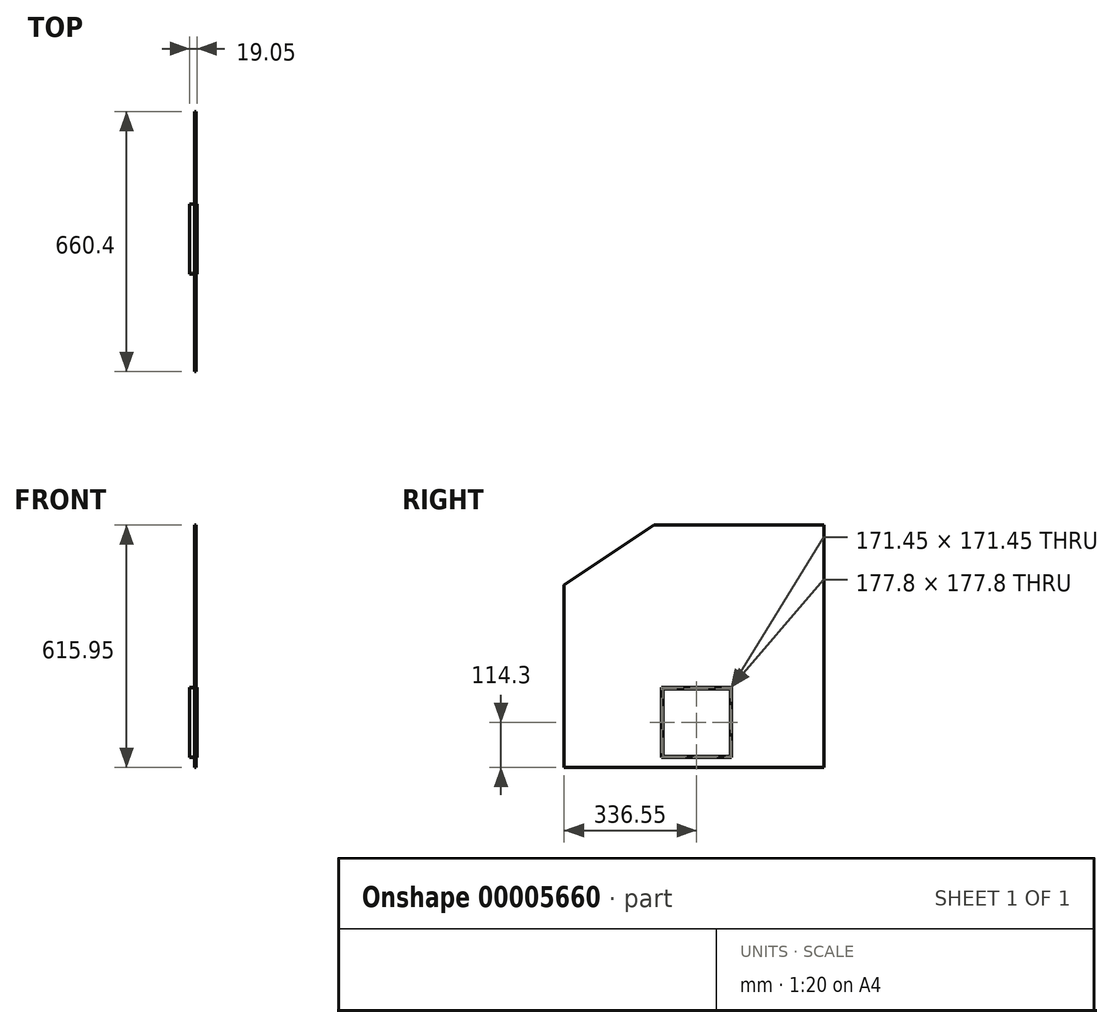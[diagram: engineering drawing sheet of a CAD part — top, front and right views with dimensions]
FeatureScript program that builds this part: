
annotation { "Feature Type Name" : "Feature", "Feature Type Description" : "" }
export const myFeature = defineFeature(function(context is Context, id is Id, definition is map)
    precondition{}
    {
        {
            var Q0;
            Q0=qCreatedBy(makeId("Right.planeOp"),FACE);
            var sketch = newSketch(context, id + "F0", { "sketchPlane" : qUnion([Q0])});
            skLineSegment(sketch, "E0.bottom", {"start": v(0, 0) * mm, "end": v(-431.8, 0) * mm});
            skLineSegment(sketch, "E0.top", {"start": v(0, 615.95) * mm, "end": v(-431.8, 615.95) * mm});
            skLineSegment(sketch, "E0.left", {"start": v(0, 0) * mm, "end": v(0, 615.95) * mm});
            skLineSegment(sketch, "E0.right", {"start": v(-431.8, 0) * mm, "end": v(-431.8, 615.95) * mm, "construction": true});
            skLineSegment(sketch, "E1", {"start": v(-431.8, 615.95) * mm, "end": v(-660.4, 463.55) * mm});
            skLineSegment(sketch, "E2", {"start": v(-660.4, 463.55) * mm, "end": v(-431.8, 463.55) * mm, "construction": true});
            skLineSegment(sketch, "E3", {"start": v(-660.4, 463.55) * mm, "end": v(-660.4, 0) * mm});
            skLineSegment(sketch, "E4", {"start": v(-431.8, 0) * mm, "end": v(-660.4, 0) * mm});
            skLineSegment(sketch, "E5.bottom", {"start": v(-234.95, 25.4) * mm, "end": v(-412.75, 25.4) * mm});
            skLineSegment(sketch, "E5.top", {"start": v(-234.95, 203.2) * mm, "end": v(-412.75, 203.2) * mm});
            skLineSegment(sketch, "E5.left", {"start": v(-234.95, 25.4) * mm, "end": v(-234.95, 203.2) * mm});
            skLineSegment(sketch, "E5.right", {"start": v(-412.75, 25.4) * mm, "end": v(-412.75, 203.2) * mm});
            skLineSegment(sketch, "E6.bottom", {"start": v(-238.12, 200.02) * mm, "end": v(-409.58, 200.02) * mm});
            skLineSegment(sketch, "E6.top", {"start": v(-238.12, 28.57) * mm, "end": v(-409.57, 28.57) * mm});
            skLineSegment(sketch, "E6.left", {"start": v(-238.12, 200.03) * mm, "end": v(-238.12, 28.57) * mm});
            skLineSegment(sketch, "E6.right", {"start": v(-409.57, 200.02) * mm, "end": v(-409.57, 28.57) * mm});
            skSolve(sketch);
        }
        {
            var Q0;
            Q0=qSketchRegion(id+"F0",true);
            extrude(context, id + "F1", {"entities" : qUnion([Q0]), "depth" : 3.17 * mm});
        }
        {
            var Q0;
            Q0=makeQuery(id+"F0.imprint","IMPRINT",FACE,{"disambiguationData":[TD([[makeQuery(id+"F0.imprint","IMPRINT",EDGE,{"derivedFrom":sQuery(id+"F0.wireOp",EDGE,"E6.bottom")}),1.0]])]});
            extrude(context, id + "F2", {"entities" : qUnion([Q0]), "operationType" : NewBodyOperationType.REMOVE, "oppositeDirection" : true, "depth" : 25.4 * mm});
        }
        {
            var Q0;
            Q0=makeQuery(id+"F0.imprint","IMPRINT",FACE,{"disambiguationData":[TD([[makeQuery(id+"F0.imprint","IMPRINT",EDGE,{"derivedFrom":sQuery(id+"F0.wireOp",EDGE,"E5.bottom")}),-1.0]])]});
            extrude(context, id + "F3", {"entities" : qUnion([Q0]), "endBound" : BoundingType.SYMMETRIC, "depth" : 25.4 * mm});
        }
        {
            var Q0;
            Q0=makeQuery(id+"F3.opExtrude","CAP_FACE",FACE,{"disambiguationData":[OSD([sQuery(id+"F0.wireOp",EDGE,"E5.bottom"),sQuery(id+"F0.wireOp",EDGE,"E5.top"),sQuery(id+"F0.wireOp",EDGE,"E5.left"),sQuery(id+"F0.wireOp",EDGE,"E5.right"),sQuery(id+"F0.wireOp",EDGE,"E6.bottom"),sQuery(id+"F0.wireOp",EDGE,"E6.top"),sQuery(id+"F0.wireOp",EDGE,"E6.left"),sQuery(id+"F0.wireOp",EDGE,"E6.right")])],"isStart":false});
            extrude(context, id + "F4", {"entities" : qUnion([Q0]), "operationType" : NewBodyOperationType.REMOVE, "oppositeDirection" : true, "depth" : 6.35 * mm});
        }
    });
